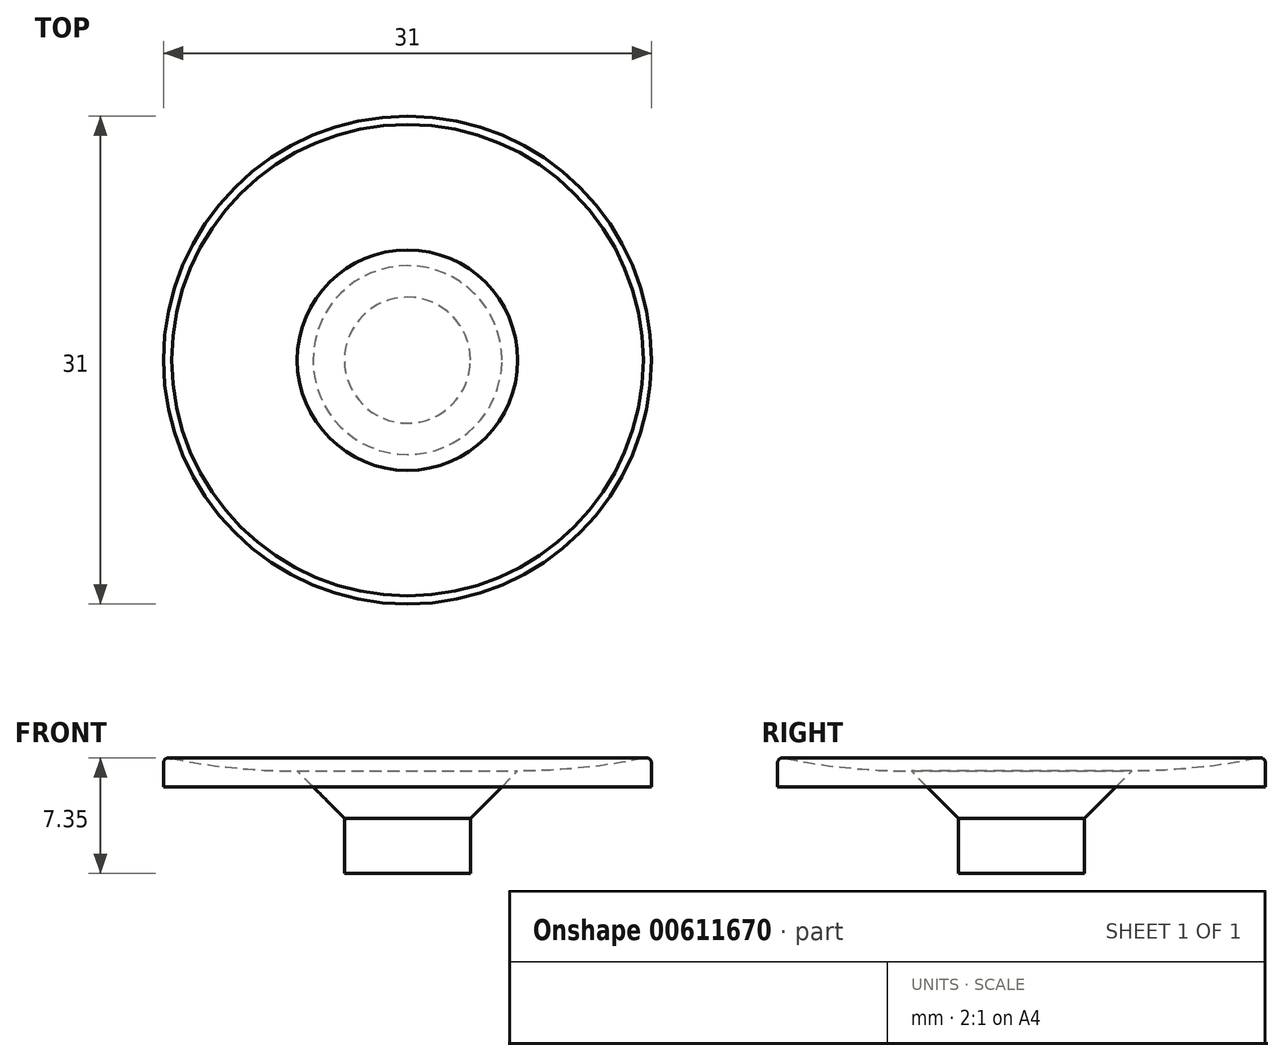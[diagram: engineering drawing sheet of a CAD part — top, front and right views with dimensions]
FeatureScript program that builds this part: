
annotation { "Feature Type Name" : "Feature", "Feature Type Description" : "" }
export const myFeature = defineFeature(function(context is Context, id is Id, definition is map)
    precondition{}
    {
        {
            var Q0;
            Q0=qCreatedBy(makeId("Front.planeOp"),FACE);
            var sketch = newSketch(context, id + "F0", { "sketchPlane" : qUnion([Q0])});
            skLineSegment(sketch, "E0", {"start": v(0, 0) * mm, "end": v(0, -3) * mm});
            skLineSegment(sketch, "E1", {"start": v(0, -3) * mm, "end": v(4, -3) * mm});
            skLineSegment(sketch, "E2", {"start": v(0, 0) * mm, "end": v(0, 2.5) * mm});
            skLineSegment(sketch, "E3", {"start": v(4, -3) * mm, "end": v(4, 0.5) * mm});
            skLineSegment(sketch, "E4", {"start": v(0, 2.5) * mm, "end": v(4, 2.5) * mm});
            skLineSegment(sketch, "E5", {"start": v(4, 2.5) * mm, "end": v(6, 2.5) * mm});
            skLineSegment(sketch, "E6", {"start": v(4, 2.5) * mm, "end": v(15.5, 2.5) * mm});
            skLineSegment(sketch, "E7", {"start": v(4, 0.5) * mm, "end": v(4, 2.5) * mm, "construction": true});
            skLineSegment(sketch, "E8", {"start": v(4, 0.5) * mm, "end": v(6, 2.5) * mm});
            skLineSegment(sketch, "E9", {"start": v(0, 3.5) * mm, "end": v(7, 3.5) * mm});
            skLineSegment(sketch, "E10", {"start": v(6, 2.5) * mm, "end": v(7, 3.5) * mm});
            skLineSegment(sketch, "E11", {"start": v(0, 3.5) * mm, "end": v(0, 2.5) * mm});
            skLineSegment(sketch, "E12", {"start": v(15.5, 2.5) * mm, "end": v(15.5, 4) * mm});
            skArc(sketch, "E13", {"start": v(15.5, 4) * mm, "mid": v(15.32, 4.3) * mm, "end": v(14.97, 4.3) * mm});
            skLineSegment(sketch, "E14", {"start": v(14.97, 4.3) * mm, "end": v(15.15, 4) * mm, "construction": true});
            skLineSegment(sketch, "E15", {"start": v(15.15, 4) * mm, "end": v(15.5, 4) * mm, "construction": true});
            skArc(sketch, "E16", {"start": v(7, 3.5) * mm, "mid": v(11, 3.7) * mm, "end": v(14.97, 4.3) * mm});
            skSolve(sketch);
        }
        {
            var Q0;
            {var subQ0=sQuery(id+"F0.wireOp",EDGE,"E10");Q0=makeQuery(id+"F0.imprint","IMPRINT",FACE,{"disambiguationData":[TD([[makeQuery(id+"F0.imprint","IMPRINT",EDGE,{"derivedFrom":subQ0}),-1.0]])]});}
            var Q1;
            Q1=sQuery(id+"F0.wireOp",EDGE,"E2");
            revolve(context, id + "F1", {"surfaceOperationType" : NewSurfaceOperationType.NEW, "entities" : qUnion([Q0]), "axis" : qUnion([Q1]), "revolveType" : RevolveType.FULL});
        }
        {
            var Q0;
            {var subQ1=sQuery(id+"F0.wireOp",EDGE,"E4");Q0=makeQuery(id+"F0.imprint","IMPRINT",FACE,{"disambiguationData":[TD([[makeQuery(id+"F0.imprint","IMPRINT",EDGE,{"derivedFrom":subQ1}),1.0]])]});}
            var Q1;
            Q1=makeQuery(id+"F0.imprint","IMPRINT",FACE,{"disambiguationData":[TD([[makeQuery(id+"F0.imprint","IMPRINT",EDGE,{"derivedFrom":sQuery(id+"F0.wireOp",EDGE,"E0")}),1.0]])]});
            var Q2;
            Q2=sQuery(id+"F0.wireOp",EDGE,"E2");
            revolve(context, id + "F2", {"surfaceOperationType" : NewSurfaceOperationType.NEW, "entities" : qUnion([Q0, Q1]), "axis" : qUnion([Q2]), "revolveType" : RevolveType.FULL});
        }
    });
